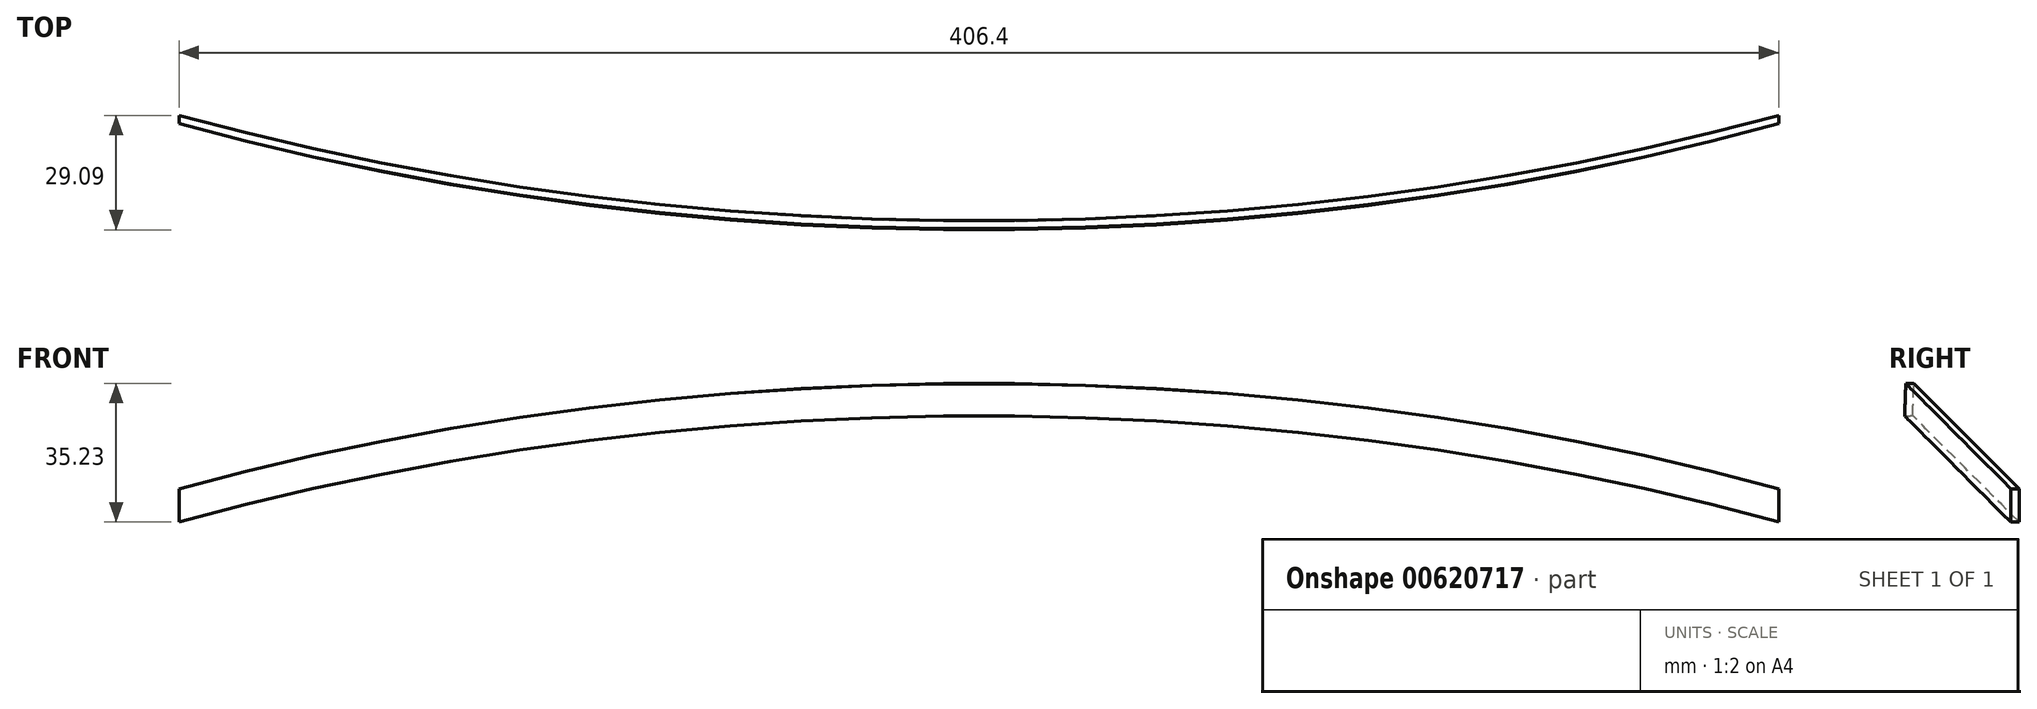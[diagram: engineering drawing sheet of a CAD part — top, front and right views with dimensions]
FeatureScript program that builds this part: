
annotation { "Feature Type Name" : "Feature", "Feature Type Description" : "" }
export const myFeature = defineFeature(function(context is Context, id is Id, definition is map)
    precondition{}
    {
        {
            var Q0;
            Q0=qCreatedBy(makeId("Top.planeOp"),FACE);
            var Q1;
            Q1=qCreatedBy(makeId("Front.planeOp"),FACE);
            cPlane(context, id + "F0", {"entities" : qUnion([Q0, Q1]), "cplaneType" : CPlaneType.MID_PLANE, "offset" : 25.4 * mm, "width" : 152.4 * mm, "height" : 152.4 * mm});
        }
        {
            var Q0;
            Q0=qCreatedBy(id+"F0.planeOp",FACE);
            var sketch = newSketch(context, id + "F1", { "sketchPlane" : qUnion([Q0])});
            skArc(sketch, "E0", {"start": v(203.2, -72.8) * mm, "mid": v(0, -34.54) * mm, "end": v(-203.2, -72.8) * mm});
            skSolve(sketch);
        }
        {
            var Q0;
            Q0=qCreatedBy(makeId("Right.planeOp"),FACE);
            cPlane(context, id + "F2", {"entities" : qUnion([Q0]), "cplaneType" : CPlaneType.OFFSET, "offset" : 203.2 * mm, "width" : 152.4 * mm, "height" : 152.4 * mm});
        }
        {
            var Q0;
            Q0=qCreatedBy(id+"F2.planeOp",FACE);
            var sketch = newSketch(context, id + "F3", { "sketchPlane" : qUnion([Q0])});
            skLineSegment(sketch, "E1.bottom", {"start": v(51.47, -51.47) * mm, "end": v(49.36, -51.47) * mm});
            skLineSegment(sketch, "E1.top", {"start": v(51.47, -43) * mm, "end": v(49.36, -43) * mm});
            skLineSegment(sketch, "E1.left", {"start": v(51.47, -51.47) * mm, "end": v(51.47, -43) * mm});
            skLineSegment(sketch, "E1.right", {"start": v(49.36, -51.47) * mm, "end": v(49.36, -43) * mm});
            skSolve(sketch);
        }
        {
            var Q0;
            Q0=qCreatedBy(makeId("Right.planeOp"),FACE);
            cPlane(context, id + "F4", {"entities" : qUnion([Q0]), "cplaneType" : CPlaneType.OFFSET, "offset" : 203.2 * mm, "oppositeDirection" : true, "width" : 152.4 * mm, "height" : 152.4 * mm});
        }
        {
            var Q0;
            Q0=qCreatedBy(id+"F4.planeOp",FACE);
            var sketch = newSketch(context, id + "F5", { "sketchPlane" : qUnion([Q0])});
            skLineSegment(sketch, "E2.bottom", {"start": v(366.8, -354.06) * mm, "end": v(-144.55, -354.06) * mm});
            skLineSegment(sketch, "E2.top", {"start": v(366.8, 112.08) * mm, "end": v(-144.55, 112.08) * mm});
            skLineSegment(sketch, "E2.left", {"start": v(366.8, -354.06) * mm, "end": v(366.8, 112.08) * mm});
            skLineSegment(sketch, "E2.right", {"start": v(-144.55, -354.06) * mm, "end": v(-144.55, 112.08) * mm});
            skSolve(sketch);
        }
        {
            var Q0;
            Q0=makeQuery(id+"F3.imprint","IMPRINT",FACE,{"disambiguationData":[TD([[makeQuery(id+"F3.imprint","IMPRINT",EDGE,{"derivedFrom":sQuery(id+"F3.wireOp",EDGE,"E1.bottom")}),-1.0]])]});
            var Q1;
            Q1=sQuery(id+"F1.wireOp",EDGE,"E0");
            sweep(context, id + "F6", {"profiles" : qUnion([Q0]), "path" : qUnion([Q1])});
        }
        {
            var Q0;
            Q0=makeQuery(id+"F5.imprint","IMPRINT",FACE,{"disambiguationData":[TD([[makeQuery(id+"F5.imprint","IMPRINT",EDGE,{"derivedFrom":sQuery(id+"F5.wireOp",EDGE,"E2.bottom")}),-1.0]])]});
            extrude(context, id + "F7", {"entities" : qUnion([Q0]), "operationType" : NewBodyOperationType.REMOVE, "endBound" : BoundingType.THROUGH_ALL, "oppositeDirection" : true, "depth" : 25.4 * mm, "offsetDistance" : 25.4 * mm});
        }
    });
